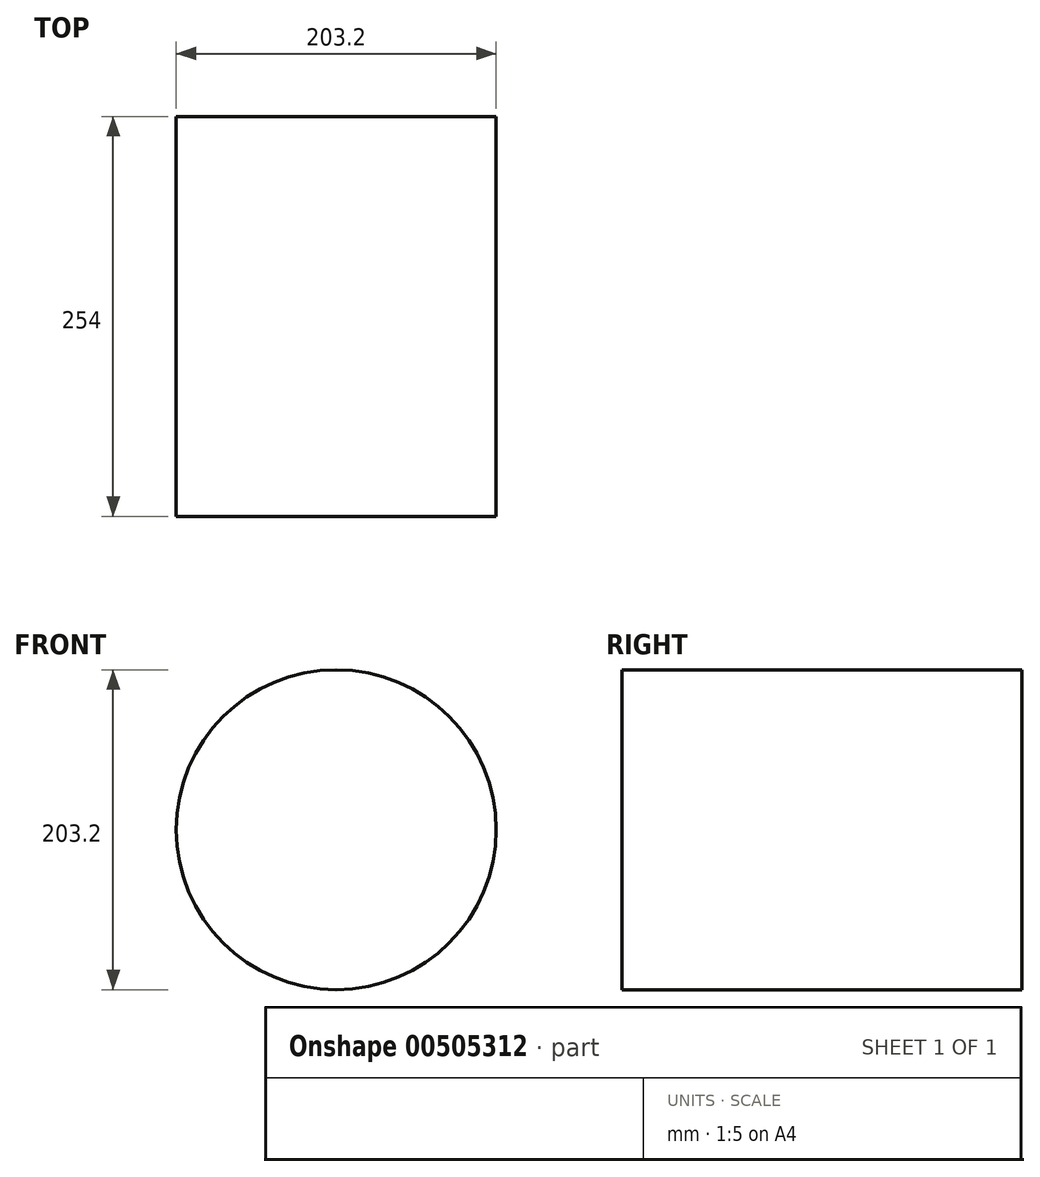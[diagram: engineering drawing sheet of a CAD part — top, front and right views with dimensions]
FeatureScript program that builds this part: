
annotation { "Feature Type Name" : "Feature", "Feature Type Description" : "" }
export const myFeature = defineFeature(function(context is Context, id is Id, definition is map)
    precondition{}
    {
        {
            var Q0;
            Q0=qCreatedBy(makeId("Front.planeOp"),FACE);
            var sketch = newSketch(context, id + "F0", { "sketchPlane" : qUnion([Q0])});
            skCircle(sketch, "E0", {"center": v(0, 0) * mm, "radius": 101.6 * mm});
            skSolve(sketch);
        }
        {
            var Q0;
            Q0 = qSketchRegion(id + "F0", true);
            extrude(context, id + "F1", {"entities" : qUnion([Q0]), "depth" : 254 * mm});
        }
    });
